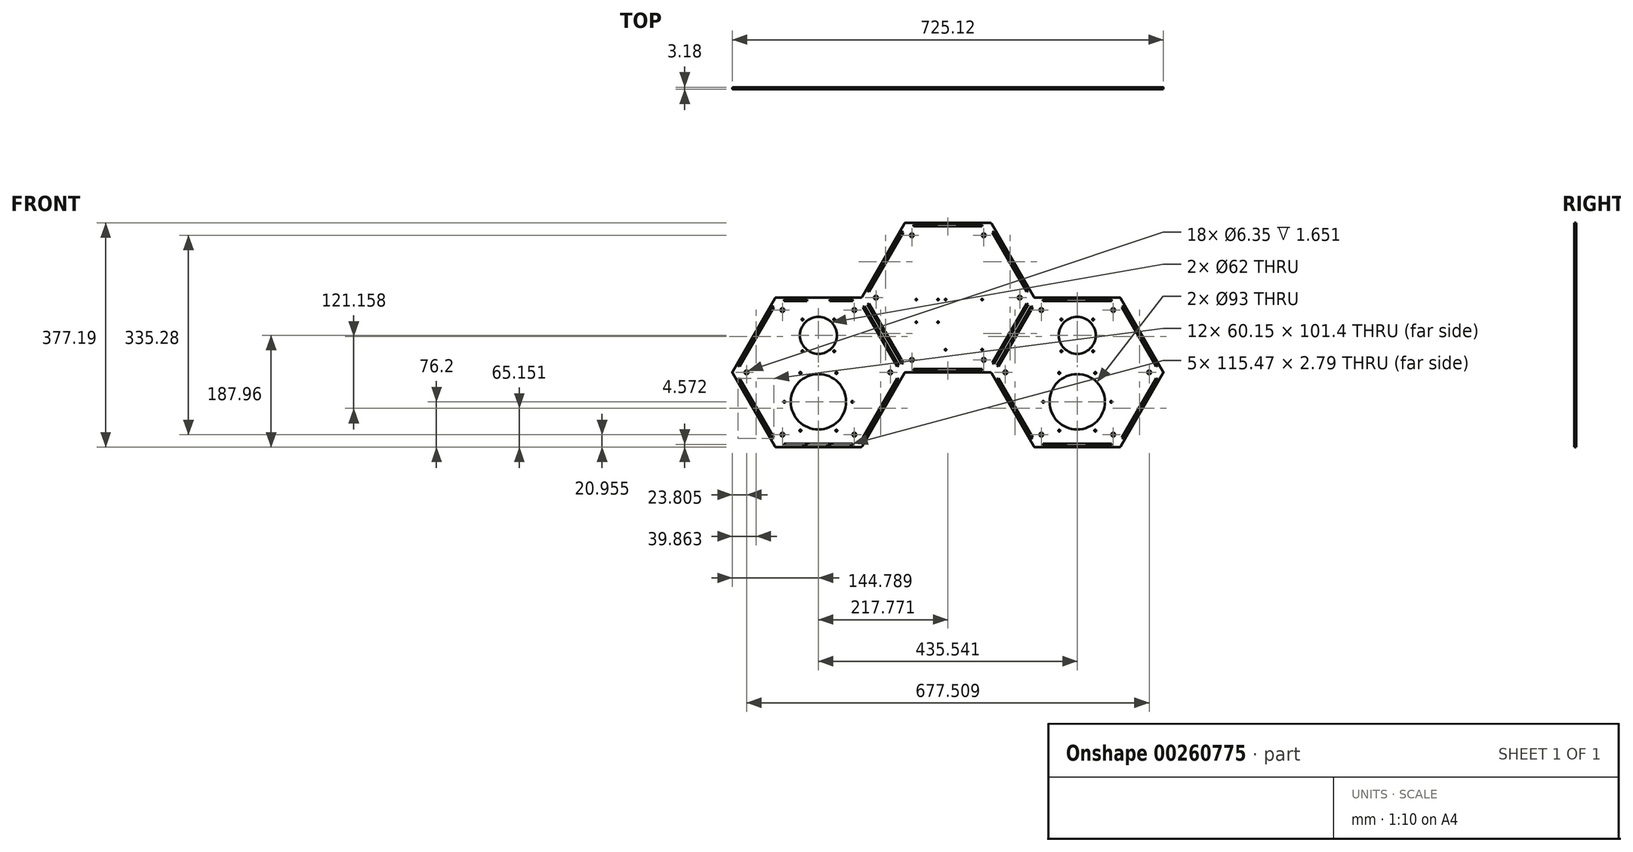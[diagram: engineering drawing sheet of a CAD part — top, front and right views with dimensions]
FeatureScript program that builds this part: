
annotation { "Feature Type Name" : "Feature", "Feature Type Description" : "" }
export const myFeature = defineFeature(function(context is Context, id is Id, definition is map)
    precondition{}
    {
        {
            var Q0;
            Q0=qCreatedBy(makeId("Front.planeOp"),FACE);
            var sketch = newSketch(context, id + "F0", { "sketchPlane" : qUnion([Q0])});
            skCircle(sketch, "E0.cCircle", {"center": v(0, 0) * mm, "radius": 125.73 * mm, "construction": true});
            skLineSegment(sketch, "E0.1", {"start": v(71.12, -125.73) * mm, "end": v(-71.12, -125.73) * mm});
            skLineSegment(sketch, "E0.3", {"start": v(-144.45, 1.27) * mm, "end": v(-73.32, 124.46) * mm});
            skLineSegment(sketch, "E0.4", {"start": v(-71.12, 125.73) * mm, "end": v(71.12, 125.73) * mm});
            skLineSegment(sketch, "E0.5", {"start": v(73.32, 124.46) * mm, "end": v(144.45, 1.27) * mm});
            skCircle(sketch, "E1.cCircle", {"center": v(-217.77, -125.73) * mm, "radius": 125.73 * mm, "construction": true});
            skLineSegment(sketch, "E1.0", {"start": v(-146.65, -251.46) * mm, "end": v(-288.9, -251.46) * mm});
            skLineSegment(sketch, "E1.1", {"start": v(-291.1, -250.19) * mm, "end": v(-362.22, -127) * mm});
            skLineSegment(sketch, "E1.2", {"start": v(-362.22, -124.46) * mm, "end": v(-291.1, -1.27) * mm});
            skLineSegment(sketch, "E1.3", {"start": v(-288.9, 0) * mm, "end": v(-146.65, 0) * mm});
            skLineSegment(sketch, "E1.5", {"start": v(-73.32, -127) * mm, "end": v(-144.45, -250.19) * mm});
            skPoint(sketch, "E1.0.midPoint", {"position": v(-217.77, -251.46) * mm});
            skCircle(sketch, "E2.cCircle", {"center": v(217.77, -125.73) * mm, "radius": 125.73 * mm, "construction": true});
            skLineSegment(sketch, "E2.0", {"start": v(362.22, -127) * mm, "end": v(291.1, -250.2) * mm});
            skLineSegment(sketch, "E2.1", {"start": v(288.9, -251.46) * mm, "end": v(146.65, -251.46) * mm});
            skLineSegment(sketch, "E2.2", {"start": v(144.45, -250.2) * mm, "end": v(73.32, -127) * mm});
            skLineSegment(sketch, "E2.4", {"start": v(146.65, 0) * mm, "end": v(288.9, 0) * mm});
            skLineSegment(sketch, "E2.5", {"start": v(291.1, -1.27) * mm, "end": v(362.22, -124.46) * mm});
            skPoint(sketch, "E2.0.midPoint", {"position": v(326.66, -188.6) * mm});
            skPoint(sketch, "E3.visualSharp", {"position": v(-72.6, 125.73) * mm});
            skArc(sketch, "E3.filletArc", {"start": v(-71.12, 125.73) * mm, "mid": v(-72.4, 125.39) * mm, "end": v(-73.32, 124.46) * mm});
            skPoint(sketch, "E4.visualSharp", {"position": v(72.6, 125.73) * mm});
            skArc(sketch, "E4.filletArc", {"start": v(73.32, 124.46) * mm, "mid": v(72.4, 125.39) * mm, "end": v(71.12, 125.73) * mm});
            skPoint(sketch, "E5.visualSharp", {"position": v(145.18, 0) * mm});
            skArc(sketch, "E5.filletArc", {"start": v(144.45, 1.27) * mm, "mid": v(145.38, 0.34) * mm, "end": v(146.65, 0) * mm});
            skPoint(sketch, "E6.visualSharp", {"position": v(290.36, 0) * mm});
            skArc(sketch, "E6.filletArc", {"start": v(291.1, -1.27) * mm, "mid": v(290.16, -0.34) * mm, "end": v(288.9, 0) * mm});
            skPoint(sketch, "E7.visualSharp", {"position": v(362.95, -125.73) * mm});
            skArc(sketch, "E7.filletArc", {"start": v(362.22, -127) * mm, "mid": v(362.56, -125.73) * mm, "end": v(362.22, -124.46) * mm});
            skPoint(sketch, "E8.visualSharp", {"position": v(290.36, -251.46) * mm});
            skArc(sketch, "E8.filletArc", {"start": v(288.9, -251.46) * mm, "mid": v(290.16, -251.12) * mm, "end": v(291.1, -250.2) * mm});
            skPoint(sketch, "E9.visualSharp", {"position": v(145.18, -251.46) * mm});
            skArc(sketch, "E9.filletArc", {"start": v(144.45, -250.2) * mm, "mid": v(145.38, -251.12) * mm, "end": v(146.65, -251.46) * mm});
            skPoint(sketch, "E10.visualSharp", {"position": v(72.6, -125.73) * mm});
            skArc(sketch, "E10.filletArc", {"start": v(73.32, -127) * mm, "mid": v(72.4, -126.07) * mm, "end": v(71.12, -125.73) * mm});
            skPoint(sketch, "E11.visualSharp", {"position": v(-72.6, -125.73) * mm});
            skArc(sketch, "E11.filletArc", {"start": v(-71.12, -125.73) * mm, "mid": v(-72.4, -126.07) * mm, "end": v(-73.32, -127) * mm});
            skPoint(sketch, "E12.visualSharp", {"position": v(-145.18, -251.46) * mm});
            skArc(sketch, "E12.filletArc", {"start": v(-146.65, -251.46) * mm, "mid": v(-145.38, -251.12) * mm, "end": v(-144.45, -250.19) * mm});
            skPoint(sketch, "E13.visualSharp", {"position": v(-290.36, -251.46) * mm});
            skArc(sketch, "E13.filletArc", {"start": v(-291.1, -250.19) * mm, "mid": v(-290.16, -251.12) * mm, "end": v(-288.9, -251.46) * mm});
            skPoint(sketch, "E14.visualSharp", {"position": v(-362.95, -125.73) * mm});
            skArc(sketch, "E14.filletArc", {"start": v(-362.22, -124.46) * mm, "mid": v(-362.56, -125.73) * mm, "end": v(-362.22, -127) * mm});
            skPoint(sketch, "E15.visualSharp", {"position": v(-290.36, 0) * mm});
            skArc(sketch, "E15.filletArc", {"start": v(-288.9, 0) * mm, "mid": v(-290.16, -0.34) * mm, "end": v(-291.1, -1.27) * mm});
            skPoint(sketch, "E16.visualSharp", {"position": v(-145.18, 0) * mm});
            skArc(sketch, "E16.filletArc", {"start": v(-146.65, 0) * mm, "mid": v(-145.38, 0.34) * mm, "end": v(-144.45, 1.27) * mm});
            skCircle(sketch, "E17.cCircle", {"center": v(-217.77, -125.73) * mm, "radius": 104.78 * mm, "construction": true});
            skLineSegment(sketch, "E17.0", {"start": v(-278.26, -20.95) * mm, "end": v(-157.28, -20.96) * mm, "construction": true});
            skLineSegment(sketch, "E17.1", {"start": v(-157.28, -20.95) * mm, "end": v(-96.79, -125.73) * mm, "construction": true});
            skLineSegment(sketch, "E17.2", {"start": v(-96.79, -125.73) * mm, "end": v(-157.28, -230.5) * mm, "construction": true});
            skLineSegment(sketch, "E17.3", {"start": v(-157.28, -230.5) * mm, "end": v(-278.26, -230.5) * mm, "construction": true});
            skLineSegment(sketch, "E17.4", {"start": v(-278.26, -230.5) * mm, "end": v(-338.75, -125.73) * mm, "construction": true});
            skLineSegment(sketch, "E17.5", {"start": v(-338.75, -125.73) * mm, "end": v(-278.26, -20.96) * mm, "construction": true});
            skPoint(sketch, "E17.0.midPoint", {"position": v(-217.77, -20.96) * mm});
            skCircle(sketch, "E18.cCircle", {"center": v(0, 0) * mm, "radius": 104.78 * mm, "construction": true});
            skLineSegment(sketch, "E18.0", {"start": v(60.5, 104.78) * mm, "end": v(120.98, 0) * mm, "construction": true});
            skLineSegment(sketch, "E18.1", {"start": v(120.98, 0) * mm, "end": v(60.5, -104.77) * mm, "construction": true});
            skLineSegment(sketch, "E18.2", {"start": v(60.5, -104.77) * mm, "end": v(-60.5, -104.78) * mm, "construction": true});
            skLineSegment(sketch, "E18.3", {"start": v(-60.5, -104.78) * mm, "end": v(-120.98, 0) * mm, "construction": true});
            skLineSegment(sketch, "E18.4", {"start": v(-120.98, 0) * mm, "end": v(-60.5, 104.78) * mm, "construction": true});
            skLineSegment(sketch, "E18.5", {"start": v(-60.5, 104.77) * mm, "end": v(60.5, 104.77) * mm, "construction": true});
            skPoint(sketch, "E18.0.midPoint", {"position": v(90.74, 52.39) * mm});
            skCircle(sketch, "E19.cCircle", {"center": v(217.77, -125.73) * mm, "radius": 104.78 * mm, "construction": true});
            skLineSegment(sketch, "E19.0", {"start": v(157.28, -20.96) * mm, "end": v(278.26, -20.96) * mm, "construction": true});
            skLineSegment(sketch, "E19.1", {"start": v(278.26, -20.96) * mm, "end": v(338.75, -125.73) * mm, "construction": true});
            skLineSegment(sketch, "E19.2", {"start": v(338.75, -125.73) * mm, "end": v(278.26, -230.5) * mm, "construction": true});
            skLineSegment(sketch, "E19.3", {"start": v(278.26, -230.5) * mm, "end": v(157.28, -230.5) * mm, "construction": true});
            skLineSegment(sketch, "E19.4", {"start": v(157.28, -230.5) * mm, "end": v(96.79, -125.73) * mm, "construction": true});
            skLineSegment(sketch, "E19.5", {"start": v(96.79, -125.73) * mm, "end": v(157.28, -20.96) * mm, "construction": true});
            skPoint(sketch, "E19.0.midPoint", {"position": v(217.77, -20.96) * mm});
            skCircle(sketch, "E20", {"center": v(-278.26, -20.96) * mm, "radius": 3.18 * mm});
            skCircle(sketch, "E21", {"center": v(-157.28, -20.95) * mm, "radius": 3.18 * mm});
            skCircle(sketch, "E22", {"center": v(-338.75, -125.73) * mm, "radius": 3.18 * mm});
            skCircle(sketch, "E23", {"center": v(-278.26, -230.5) * mm, "radius": 3.18 * mm});
            skCircle(sketch, "E24", {"center": v(-157.28, -230.5) * mm, "radius": 3.18 * mm});
            skCircle(sketch, "E25", {"center": v(-96.79, -125.73) * mm, "radius": 3.18 * mm});
            skCircle(sketch, "E26", {"center": v(-60.5, -104.78) * mm, "radius": 3.18 * mm});
            skCircle(sketch, "E27", {"center": v(-120.98, 0) * mm, "radius": 3.18 * mm});
            skCircle(sketch, "E28", {"center": v(-60.5, 104.77) * mm, "radius": 3.18 * mm});
            skCircle(sketch, "E29", {"center": v(60.5, 104.77) * mm, "radius": 3.18 * mm});
            skCircle(sketch, "E30", {"center": v(120.98, 0) * mm, "radius": 3.18 * mm});
            skCircle(sketch, "E31", {"center": v(60.5, -104.77) * mm, "radius": 3.18 * mm});
            skCircle(sketch, "E32", {"center": v(96.79, -125.73) * mm, "radius": 3.18 * mm});
            skCircle(sketch, "E33", {"center": v(157.28, -20.96) * mm, "radius": 3.18 * mm});
            skCircle(sketch, "E34", {"center": v(278.26, -20.96) * mm, "radius": 3.18 * mm});
            skCircle(sketch, "E35", {"center": v(338.75, -125.73) * mm, "radius": 3.18 * mm});
            skCircle(sketch, "E36", {"center": v(278.26, -230.5) * mm, "radius": 3.18 * mm});
            skCircle(sketch, "E37", {"center": v(157.28, -230.5) * mm, "radius": 3.18 * mm});
            skSolve(sketch);
        }
        {
            var Q0;
            Q0=makeQuery(id+"F0.imprint","IMPRINT",FACE,{"disambiguationData":[TD([[makeQuery(id+"F0.imprint","IMPRINT",EDGE,{"derivedFrom":sQuery(id+"F0.wireOp",EDGE,"E0.1")}),-1.0]])]});
            extrude(context, id + "F1", {"entities" : qUnion([Q0]), "depth" : 3.17 * mm});
        }
        {
            var Q0;
            Q0=makeQuery(id+"F0.imprint","IMPRINT",FACE,{"disambiguationData":[TD([[makeQuery(id+"F0.imprint","IMPRINT",EDGE,{"derivedFrom":sQuery(id+"F0.wireOp",EDGE,"E30")}),1.0]])]});
            var Q1;
            Q1=makeQuery(id+"F0.imprint","IMPRINT",FACE,{"disambiguationData":[TD([[makeQuery(id+"F0.imprint","IMPRINT",EDGE,{"derivedFrom":sQuery(id+"F0.wireOp",EDGE,"E33")}),1.0]])]});
            var Q2;
            Q2=makeQuery(id+"F0.imprint","IMPRINT",FACE,{"disambiguationData":[TD([[makeQuery(id+"F0.imprint","IMPRINT",EDGE,{"derivedFrom":sQuery(id+"F0.wireOp",EDGE,"E34")}),1.0]])]});
            var Q3;
            Q3=makeQuery(id+"F0.imprint","IMPRINT",FACE,{"disambiguationData":[TD([[makeQuery(id+"F0.imprint","IMPRINT",EDGE,{"derivedFrom":sQuery(id+"F0.wireOp",EDGE,"E35")}),1.0]])]});
            var Q4;
            Q4=makeQuery(id+"F0.imprint","IMPRINT",FACE,{"disambiguationData":[TD([[makeQuery(id+"F0.imprint","IMPRINT",EDGE,{"derivedFrom":sQuery(id+"F0.wireOp",EDGE,"E36")}),1.0]])]});
            var Q5;
            Q5=makeQuery(id+"F0.imprint","IMPRINT",FACE,{"disambiguationData":[TD([[makeQuery(id+"F0.imprint","IMPRINT",EDGE,{"derivedFrom":sQuery(id+"F0.wireOp",EDGE,"E37")}),1.0]])]});
            var Q6;
            Q6=makeQuery(id+"F0.imprint","IMPRINT",FACE,{"disambiguationData":[TD([[makeQuery(id+"F0.imprint","IMPRINT",EDGE,{"derivedFrom":sQuery(id+"F0.wireOp",EDGE,"E32")}),1.0]])]});
            var Q7;
            Q7=makeQuery(id+"F0.imprint","IMPRINT",FACE,{"disambiguationData":[TD([[makeQuery(id+"F0.imprint","IMPRINT",EDGE,{"derivedFrom":sQuery(id+"F0.wireOp",EDGE,"E31")}),1.0]])]});
            var Q8;
            Q8=makeQuery(id+"F0.imprint","IMPRINT",FACE,{"disambiguationData":[TD([[makeQuery(id+"F0.imprint","IMPRINT",EDGE,{"derivedFrom":sQuery(id+"F0.wireOp",EDGE,"E26")}),1.0]])]});
            var Q9;
            Q9=makeQuery(id+"F0.imprint","IMPRINT",FACE,{"disambiguationData":[TD([[makeQuery(id+"F0.imprint","IMPRINT",EDGE,{"derivedFrom":sQuery(id+"F0.wireOp",EDGE,"E25")}),1.0]])]});
            var Q10;
            Q10=makeQuery(id+"F0.imprint","IMPRINT",FACE,{"disambiguationData":[TD([[makeQuery(id+"F0.imprint","IMPRINT",EDGE,{"derivedFrom":sQuery(id+"F0.wireOp",EDGE,"E24")}),1.0]])]});
            var Q11;
            Q11=makeQuery(id+"F0.imprint","IMPRINT",FACE,{"disambiguationData":[TD([[makeQuery(id+"F0.imprint","IMPRINT",EDGE,{"derivedFrom":sQuery(id+"F0.wireOp",EDGE,"E23")}),1.0]])]});
            var Q12;
            Q12=makeQuery(id+"F0.imprint","IMPRINT",FACE,{"disambiguationData":[TD([[makeQuery(id+"F0.imprint","IMPRINT",EDGE,{"derivedFrom":sQuery(id+"F0.wireOp",EDGE,"E22")}),1.0]])]});
            var Q13;
            Q13=makeQuery(id+"F0.imprint","IMPRINT",FACE,{"disambiguationData":[TD([[makeQuery(id+"F0.imprint","IMPRINT",EDGE,{"derivedFrom":sQuery(id+"F0.wireOp",EDGE,"E20")}),1.0]])]});
            var Q14;
            Q14=makeQuery(id+"F0.imprint","IMPRINT",FACE,{"disambiguationData":[TD([[makeQuery(id+"F0.imprint","IMPRINT",EDGE,{"derivedFrom":sQuery(id+"F0.wireOp",EDGE,"E21")}),1.0]])]});
            var Q15;
            Q15=makeQuery(id+"F0.imprint","IMPRINT",FACE,{"disambiguationData":[TD([[makeQuery(id+"F0.imprint","IMPRINT",EDGE,{"derivedFrom":sQuery(id+"F0.wireOp",EDGE,"E27")}),1.0]])]});
            var Q16;
            Q16=makeQuery(id+"F0.imprint","IMPRINT",FACE,{"disambiguationData":[TD([[makeQuery(id+"F0.imprint","IMPRINT",EDGE,{"derivedFrom":sQuery(id+"F0.wireOp",EDGE,"E28")}),1.0]])]});
            var Q17;
            Q17=makeQuery(id+"F0.imprint","IMPRINT",FACE,{"disambiguationData":[TD([[makeQuery(id+"F0.imprint","IMPRINT",EDGE,{"derivedFrom":sQuery(id+"F0.wireOp",EDGE,"E29")}),1.0]])]});
            extrude(context, id + "F2", {"entities" : qUnion([Q0, Q1, Q2, Q3, Q4, Q5, Q6, Q7, Q8, Q9, Q10, Q11, Q12, Q13, Q14, Q15, Q16, Q17]), "operationType" : NewBodyOperationType.ADD, "depth" : 1.52 * mm});
        }
        {
            var Q0;
            Q0=makeQuery(id+"F1.opExtrude","CAP_FACE",FACE,{"disambiguationData":[OSD([sQuery(id+"F0.wireOp",EDGE,"E0.1"),sQuery(id+"F0.wireOp",EDGE,"E0.3"),sQuery(id+"F0.wireOp",EDGE,"E0.4"),sQuery(id+"F0.wireOp",EDGE,"E0.5"),sQuery(id+"F0.wireOp",EDGE,"E1.0"),sQuery(id+"F0.wireOp",EDGE,"E1.1"),sQuery(id+"F0.wireOp",EDGE,"E1.2"),sQuery(id+"F0.wireOp",EDGE,"E1.3"),sQuery(id+"F0.wireOp",EDGE,"E1.5"),sQuery(id+"F0.wireOp",EDGE,"E2.0"),sQuery(id+"F0.wireOp",EDGE,"E2.1"),sQuery(id+"F0.wireOp",EDGE,"E2.2"),sQuery(id+"F0.wireOp",EDGE,"E2.4"),sQuery(id+"F0.wireOp",EDGE,"E2.5"),sQuery(id+"F0.wireOp",EDGE,"E3.filletArc"),sQuery(id+"F0.wireOp",EDGE,"E4.filletArc"),sQuery(id+"F0.wireOp",EDGE,"E5.filletArc"),sQuery(id+"F0.wireOp",EDGE,"E6.filletArc"),sQuery(id+"F0.wireOp",EDGE,"E7.filletArc"),sQuery(id+"F0.wireOp",EDGE,"E8.filletArc"),sQuery(id+"F0.wireOp",EDGE,"E9.filletArc"),sQuery(id+"F0.wireOp",EDGE,"E10.filletArc"),sQuery(id+"F0.wireOp",EDGE,"E11.filletArc"),sQuery(id+"F0.wireOp",EDGE,"E12.filletArc"),sQuery(id+"F0.wireOp",EDGE,"E13.filletArc"),sQuery(id+"F0.wireOp",EDGE,"E14.filletArc"),sQuery(id+"F0.wireOp",EDGE,"E15.filletArc"),sQuery(id+"F0.wireOp",EDGE,"E16.filletArc"),sQuery(id+"F0.wireOp",EDGE,"E20"),sQuery(id+"F0.wireOp",EDGE,"E21"),sQuery(id+"F0.wireOp",EDGE,"E22"),sQuery(id+"F0.wireOp",EDGE,"E23"),sQuery(id+"F0.wireOp",EDGE,"E24"),sQuery(id+"F0.wireOp",EDGE,"E25"),sQuery(id+"F0.wireOp",EDGE,"E26"),sQuery(id+"F0.wireOp",EDGE,"E27"),sQuery(id+"F0.wireOp",EDGE,"E28"),sQuery(id+"F0.wireOp",EDGE,"E29"),sQuery(id+"F0.wireOp",EDGE,"E30"),sQuery(id+"F0.wireOp",EDGE,"E31"),sQuery(id+"F0.wireOp",EDGE,"E32"),sQuery(id+"F0.wireOp",EDGE,"E33"),sQuery(id+"F0.wireOp",EDGE,"E34"),sQuery(id+"F0.wireOp",EDGE,"E35"),sQuery(id+"F0.wireOp",EDGE,"E36"),sQuery(id+"F0.wireOp",EDGE,"E37")])],"isStart":false});
            var sketch = newSketch(context, id + "F3", { "sketchPlane" : qUnion([Q0])});
            skPoint(sketch, "E38", {"position": v(-217.77, -127) * mm});
            skCircle(sketch, "E39", {"center": v(-217.77, -63.5) * mm, "radius": 31 * mm});
            skCircle(sketch, "E40", {"center": v(-217.77, -175.26) * mm, "radius": 46.5 * mm});
            skLineSegment(sketch, "E41", {"start": v(-295.75, -175.26) * mm, "end": v(-133.33, -175.26) * mm, "construction": true});
            skCircle(sketch, "E42", {"center": v(-217.77, -175.26) * mm, "radius": 61.65 * mm, "construction": true});
            skCircle(sketch, "E43", {"center": v(-217.77, -175.26) * mm, "radius": 57.15 * mm, "construction": true});
            skCircle(sketch, "E44", {"center": v(-160.62, -175.26) * mm, "radius": 1.52 * mm});
            skLineSegment(sketch, "E45", {"start": v(-217.77, -175.26) * mm, "end": v(-217.77, -149.19) * mm, "construction": true});
            skLineSegment(sketch, "E46", {"start": v(-217.77, -175.26) * mm, "end": v(-187.49, -126.8) * mm, "construction": true});
            skLineSegment(sketch, "E47", {"start": v(-217.77, -175.26) * mm, "end": v(-187.49, -223.73) * mm, "construction": true});
            skCircle(sketch, "E48", {"center": v(-187.49, -126.8) * mm, "radius": 1.52 * mm});
            skCircle(sketch, "E49", {"center": v(-187.49, -223.73) * mm, "radius": 1.52 * mm});
            skCircle(sketch, "E50.MirrorC", {"center": v(-248.06, -126.8) * mm, "radius": 1.52 * mm});
            skCircle(sketch, "E51.MirrorC", {"center": v(-248.06, -223.73) * mm, "radius": 1.52 * mm});
            skCircle(sketch, "E52.MirrorC", {"center": v(-274.92, -175.26) * mm, "radius": 1.52 * mm});
            skCircle(sketch, "E53", {"center": v(-217.77, -63.5) * mm, "radius": 37.72 * mm, "construction": true});
            skLineSegment(sketch, "E54", {"start": v(-217.77, -63.5) * mm, "end": v(-244.44, -36.83) * mm, "construction": true});
            skCircle(sketch, "E55", {"center": v(-244.44, -36.83) * mm, "radius": 1.52 * mm});
            skCircle(sketch, "E56", {"center": v(-244.44, -90.17) * mm, "radius": 1.52 * mm});
            skCircle(sketch, "E57", {"center": v(-191.1, -90.17) * mm, "radius": 1.52 * mm});
            skCircle(sketch, "E58", {"center": v(-191.1, -36.83) * mm, "radius": 1.52 * mm});
            skLineSegment(sketch, "E59", {"start": v(-244.44, -36.83) * mm, "end": v(-191.1, -36.83) * mm, "construction": true});
            skCircle(sketch, "E60.MirrorC", {"center": v(160.62, -175.26) * mm, "radius": 1.52 * mm});
            skCircle(sketch, "E61.MirrorC", {"center": v(187.49, -223.73) * mm, "radius": 1.52 * mm});
            skCircle(sketch, "E62.MirrorC", {"center": v(248.06, -223.73) * mm, "radius": 1.52 * mm});
            skCircle(sketch, "E63.MirrorC", {"center": v(274.92, -175.26) * mm, "radius": 1.52 * mm});
            skCircle(sketch, "E64.MirrorC", {"center": v(187.49, -126.8) * mm, "radius": 1.52 * mm});
            skCircle(sketch, "E65.MirrorC", {"center": v(248.06, -126.8) * mm, "radius": 1.52 * mm});
            skCircle(sketch, "E66.MirrorC", {"center": v(217.77, -175.26) * mm, "radius": 46.5 * mm});
            skCircle(sketch, "E67.MirrorC", {"center": v(244.44, -90.17) * mm, "radius": 1.52 * mm});
            skCircle(sketch, "E68.MirrorC", {"center": v(191.1, -90.17) * mm, "radius": 1.52 * mm});
            skCircle(sketch, "E69.MirrorC", {"center": v(191.1, -36.83) * mm, "radius": 1.52 * mm});
            skCircle(sketch, "E70.MirrorC", {"center": v(217.77, -63.5) * mm, "radius": 31 * mm});
            skCircle(sketch, "E71.MirrorC", {"center": v(244.44, -36.83) * mm, "radius": 1.52 * mm});
            skSolve(sketch);
        }
        {
            var Q0;
            Q0 = qSketchRegion(id + "F3", true);
            extrude(context, id + "F4", {"entities" : qUnion([Q0]), "operationType" : NewBodyOperationType.REMOVE, "endBound" : BoundingType.THROUGH_ALL, "oppositeDirection" : true, "depth" : 25.4 * mm});
        }
        {
            var Q0;
            Q0=makeQuery(id+"F1.opExtrude","CAP_FACE",FACE,{"disambiguationData":[OSD([sQuery(id+"F0.wireOp",EDGE,"E0.1"),sQuery(id+"F0.wireOp",EDGE,"E0.3"),sQuery(id+"F0.wireOp",EDGE,"E0.4"),sQuery(id+"F0.wireOp",EDGE,"E0.5"),sQuery(id+"F0.wireOp",EDGE,"E1.0"),sQuery(id+"F0.wireOp",EDGE,"E1.1"),sQuery(id+"F0.wireOp",EDGE,"E1.2"),sQuery(id+"F0.wireOp",EDGE,"E1.3"),sQuery(id+"F0.wireOp",EDGE,"E1.5"),sQuery(id+"F0.wireOp",EDGE,"E2.0"),sQuery(id+"F0.wireOp",EDGE,"E2.1"),sQuery(id+"F0.wireOp",EDGE,"E2.2"),sQuery(id+"F0.wireOp",EDGE,"E2.4"),sQuery(id+"F0.wireOp",EDGE,"E2.5"),sQuery(id+"F0.wireOp",EDGE,"E3.filletArc"),sQuery(id+"F0.wireOp",EDGE,"E4.filletArc"),sQuery(id+"F0.wireOp",EDGE,"E5.filletArc"),sQuery(id+"F0.wireOp",EDGE,"E6.filletArc"),sQuery(id+"F0.wireOp",EDGE,"E7.filletArc"),sQuery(id+"F0.wireOp",EDGE,"E8.filletArc"),sQuery(id+"F0.wireOp",EDGE,"E9.filletArc"),sQuery(id+"F0.wireOp",EDGE,"E10.filletArc"),sQuery(id+"F0.wireOp",EDGE,"E11.filletArc"),sQuery(id+"F0.wireOp",EDGE,"E12.filletArc"),sQuery(id+"F0.wireOp",EDGE,"E13.filletArc"),sQuery(id+"F0.wireOp",EDGE,"E14.filletArc"),sQuery(id+"F0.wireOp",EDGE,"E15.filletArc"),sQuery(id+"F0.wireOp",EDGE,"E16.filletArc"),sQuery(id+"F0.wireOp",EDGE,"E20"),sQuery(id+"F0.wireOp",EDGE,"E21"),sQuery(id+"F0.wireOp",EDGE,"E22"),sQuery(id+"F0.wireOp",EDGE,"E23"),sQuery(id+"F0.wireOp",EDGE,"E24"),sQuery(id+"F0.wireOp",EDGE,"E25"),sQuery(id+"F0.wireOp",EDGE,"E26"),sQuery(id+"F0.wireOp",EDGE,"E27"),sQuery(id+"F0.wireOp",EDGE,"E28"),sQuery(id+"F0.wireOp",EDGE,"E29"),sQuery(id+"F0.wireOp",EDGE,"E30"),sQuery(id+"F0.wireOp",EDGE,"E31"),sQuery(id+"F0.wireOp",EDGE,"E32"),sQuery(id+"F0.wireOp",EDGE,"E33"),sQuery(id+"F0.wireOp",EDGE,"E34"),sQuery(id+"F0.wireOp",EDGE,"E35"),sQuery(id+"F0.wireOp",EDGE,"E36"),sQuery(id+"F0.wireOp",EDGE,"E37")])],"isStart":false});
            var sketch = newSketch(context, id + "F5", { "sketchPlane" : qUnion([Q0])});
            skPoint(sketch, "E72", {"position": v(-217.77, -125.73) * mm});
            skCircle(sketch, "E73.cCircle", {"center": v(-217.77, -125.73) * mm, "radius": 125.73 * mm, "construction": true});
            skLineSegment(sketch, "E73.0", {"start": v(-275.7, 0) * mm, "end": v(-159.85, 0) * mm, "construction": true});
            skLineSegment(sketch, "E73.1", {"start": v(-137.85, -12.7) * mm, "end": v(-79.92, -113.03) * mm, "construction": true});
            skLineSegment(sketch, "E73.2", {"start": v(-79.92, -138.43) * mm, "end": v(-137.85, -238.76) * mm, "construction": true});
            skLineSegment(sketch, "E73.3", {"start": v(-159.85, -251.46) * mm, "end": v(-275.7, -251.46) * mm, "construction": true});
            skLineSegment(sketch, "E73.4", {"start": v(-297.7, -238.76) * mm, "end": v(-355.62, -138.43) * mm, "construction": true});
            skLineSegment(sketch, "E73.5", {"start": v(-355.62, -113.03) * mm, "end": v(-297.7, -12.7) * mm, "construction": true});
            skPoint(sketch, "E73.0.midPoint", {"position": v(-217.77, 0) * mm});
            skPoint(sketch, "E74.visualSharp", {"position": v(-290.36, 0) * mm});
            skArc(sketch, "E74.filletArc", {"start": v(-275.7, 0) * mm, "mid": v(-288.4, -3.4) * mm, "end": v(-297.7, -12.7) * mm, "construction": true});
            skPoint(sketch, "E75.visualSharp", {"position": v(-145.18, 0) * mm});
            skArc(sketch, "E75.filletArc", {"start": v(-137.85, -12.7) * mm, "mid": v(-147.15, -3.4) * mm, "end": v(-159.85, 0) * mm, "construction": true});
            skPoint(sketch, "E76.visualSharp", {"position": v(-72.6, -125.73) * mm});
            skArc(sketch, "E76.filletArc", {"start": v(-79.92, -138.43) * mm, "mid": v(-76.52, -125.73) * mm, "end": v(-79.92, -113.03) * mm, "construction": true});
            skPoint(sketch, "E77.visualSharp", {"position": v(-145.18, -251.46) * mm});
            skArc(sketch, "E77.filletArc", {"start": v(-159.85, -251.46) * mm, "mid": v(-147.15, -248.06) * mm, "end": v(-137.85, -238.76) * mm, "construction": true});
            skPoint(sketch, "E78.visualSharp", {"position": v(-290.36, -251.46) * mm});
            skArc(sketch, "E78.filletArc", {"start": v(-297.7, -238.76) * mm, "mid": v(-288.4, -248.06) * mm, "end": v(-275.7, -251.46) * mm, "construction": true});
            skPoint(sketch, "E79.visualSharp", {"position": v(-362.95, -125.73) * mm});
            skArc(sketch, "E79.filletArc", {"start": v(-355.62, -113.03) * mm, "mid": v(-359.02, -125.73) * mm, "end": v(-355.62, -138.43) * mm, "construction": true});
            skLineSegment(sketch, "E80.bottom", {"start": v(-275.5, -5.97) * mm, "end": v(-160.04, -5.97) * mm});
            skLineSegment(sketch, "E80.top", {"start": v(-275.5, -3.18) * mm, "end": v(-160.04, -3.18) * mm});
            skLineSegment(sketch, "E80.left", {"start": v(-275.5, -3.18) * mm, "end": v(-275.5, -5.97) * mm});
            skLineSegment(sketch, "E80.right", {"start": v(-160.04, -3.18) * mm, "end": v(-160.04, -5.97) * mm});
            skLineSegment(sketch, "E81.1.0", {"start": v(-352.77, -114.45) * mm, "end": v(-295.04, -14.45) * mm});
            skLineSegment(sketch, "E81.1.1", {"start": v(-352.77, -114.45) * mm, "end": v(-350.35, -115.85) * mm});
            skLineSegment(sketch, "E81.1.2", {"start": v(-350.35, -115.85) * mm, "end": v(-292.62, -15.85) * mm});
            skLineSegment(sketch, "E81.1.3", {"start": v(-295.04, -14.45) * mm, "end": v(-292.62, -15.85) * mm});
            skLineSegment(sketch, "E81.2.0", {"start": v(-295.04, -237) * mm, "end": v(-352.77, -137) * mm});
            skLineSegment(sketch, "E81.2.1", {"start": v(-295.04, -237) * mm, "end": v(-292.62, -235.61) * mm});
            skLineSegment(sketch, "E81.2.2", {"start": v(-292.62, -235.61) * mm, "end": v(-350.35, -135.61) * mm});
            skLineSegment(sketch, "E81.2.3", {"start": v(-352.77, -137) * mm, "end": v(-350.35, -135.61) * mm});
            skLineSegment(sketch, "E81.3.0", {"start": v(-160.04, -248.28) * mm, "end": v(-275.5, -248.28) * mm});
            skLineSegment(sketch, "E81.3.1", {"start": v(-160.04, -248.28) * mm, "end": v(-160.04, -245.5) * mm});
            skLineSegment(sketch, "E81.3.2", {"start": v(-160.04, -245.5) * mm, "end": v(-275.5, -245.5) * mm});
            skLineSegment(sketch, "E81.3.3", {"start": v(-275.5, -248.28) * mm, "end": v(-275.5, -245.5) * mm});
            skLineSegment(sketch, "E81.4.0", {"start": v(-82.77, -137) * mm, "end": v(-140.5, -237) * mm});
            skLineSegment(sketch, "E81.4.1", {"start": v(-82.77, -137) * mm, "end": v(-85.19, -135.61) * mm});
            skLineSegment(sketch, "E81.4.2", {"start": v(-85.19, -135.61) * mm, "end": v(-142.92, -235.61) * mm});
            skLineSegment(sketch, "E81.4.3", {"start": v(-140.5, -237) * mm, "end": v(-142.92, -235.61) * mm});
            skLineSegment(sketch, "E81.5.0", {"start": v(-140.5, -14.45) * mm, "end": v(-82.77, -114.45) * mm});
            skLineSegment(sketch, "E81.5.1", {"start": v(-140.5, -14.45) * mm, "end": v(-142.92, -15.85) * mm});
            skLineSegment(sketch, "E81.5.2", {"start": v(-142.92, -15.85) * mm, "end": v(-85.19, -115.85) * mm});
            skLineSegment(sketch, "E81.5.3", {"start": v(-82.77, -114.45) * mm, "end": v(-85.19, -115.85) * mm});
            skLineSegment(sketch, "E82.MirrorCS", {"start": v(140.5, -14.45) * mm, "end": v(142.92, -15.85) * mm});
            skLineSegment(sketch, "E83.MirrorCS", {"start": v(140.5, -14.45) * mm, "end": v(82.77, -114.45) * mm});
            skLineSegment(sketch, "E84.MirrorCS", {"start": v(142.92, -15.85) * mm, "end": v(85.19, -115.85) * mm});
            skLineSegment(sketch, "E85.MirrorCS", {"start": v(82.77, -114.45) * mm, "end": v(85.19, -115.85) * mm});
            skLineSegment(sketch, "E86.MirrorCS", {"start": v(82.77, -137) * mm, "end": v(85.19, -135.61) * mm});
            skLineSegment(sketch, "E87.MirrorCS", {"start": v(85.19, -135.61) * mm, "end": v(142.92, -235.61) * mm});
            skLineSegment(sketch, "E88.MirrorCS", {"start": v(82.77, -137) * mm, "end": v(140.5, -237) * mm});
            skLineSegment(sketch, "E89.MirrorCS", {"start": v(140.5, -237) * mm, "end": v(142.92, -235.61) * mm});
            skLineSegment(sketch, "E90.MirrorCS", {"start": v(160.04, -248.28) * mm, "end": v(160.04, -245.5) * mm});
            skLineSegment(sketch, "E91.MirrorCS", {"start": v(160.04, -248.28) * mm, "end": v(275.5, -248.28) * mm});
            skLineSegment(sketch, "E92.MirrorCS", {"start": v(160.04, -245.5) * mm, "end": v(275.5, -245.5) * mm});
            skLineSegment(sketch, "E93.MirrorCS", {"start": v(275.5, -248.28) * mm, "end": v(275.5, -245.5) * mm});
            skLineSegment(sketch, "E94.MirrorCS", {"start": v(295.04, -237) * mm, "end": v(292.62, -235.61) * mm});
            skLineSegment(sketch, "E95.MirrorCS", {"start": v(295.04, -237) * mm, "end": v(352.77, -137) * mm});
            skLineSegment(sketch, "E96.MirrorCS", {"start": v(292.62, -235.61) * mm, "end": v(350.35, -135.61) * mm});
            skLineSegment(sketch, "E97.MirrorCS", {"start": v(352.77, -137) * mm, "end": v(350.35, -135.61) * mm});
            skLineSegment(sketch, "E98.MirrorCS", {"start": v(352.77, -114.45) * mm, "end": v(350.35, -115.85) * mm});
            skLineSegment(sketch, "E99.MirrorCS", {"start": v(350.35, -115.85) * mm, "end": v(292.62, -15.85) * mm});
            skLineSegment(sketch, "E100.MirrorCS", {"start": v(352.77, -114.45) * mm, "end": v(295.04, -14.45) * mm});
            skLineSegment(sketch, "E101.MirrorCS", {"start": v(295.04, -14.45) * mm, "end": v(292.62, -15.85) * mm});
            skLineSegment(sketch, "E102.MirrorCS", {"start": v(275.5, -3.18) * mm, "end": v(275.5, -5.97) * mm});
            skLineSegment(sketch, "E103.MirrorCS", {"start": v(275.5, -5.97) * mm, "end": v(160.04, -5.97) * mm});
            skLineSegment(sketch, "E104.MirrorCS", {"start": v(275.5, -3.18) * mm, "end": v(160.04, -3.18) * mm});
            skLineSegment(sketch, "E105.MirrorCS", {"start": v(160.04, -3.18) * mm, "end": v(160.04, -5.97) * mm});
            skLineSegment(sketch, "E106.MirrorCS", {"start": v(57.74, -122.55) * mm, "end": v(57.74, -119.76) * mm});
            skLineSegment(sketch, "E107.MirrorCS", {"start": v(-57.74, -122.55) * mm, "end": v(57.74, -122.55) * mm});
            skLineSegment(sketch, "E108.MirrorCS", {"start": v(-57.74, -119.76) * mm, "end": v(57.74, -119.76) * mm});
            skLineSegment(sketch, "E109.MirrorCS", {"start": v(-57.74, -122.55) * mm, "end": v(-57.74, -119.76) * mm});
            skLineSegment(sketch, "E110.MirrorCS", {"start": v(-77.27, -111.28) * mm, "end": v(-74.85, -109.88) * mm});
            skLineSegment(sketch, "E111.MirrorCS", {"start": v(-132.58, -9.88) * mm, "end": v(-74.85, -109.88) * mm});
            skLineSegment(sketch, "E112.MirrorCS", {"start": v(-135, -11.28) * mm, "end": v(-77.27, -111.28) * mm});
            skLineSegment(sketch, "E113.MirrorCS", {"start": v(-135, -11.28) * mm, "end": v(-132.58, -9.88) * mm});
            skLineSegment(sketch, "E114.MirrorCS", {"start": v(-135, 11.28) * mm, "end": v(-132.58, 9.88) * mm});
            skLineSegment(sketch, "E115.MirrorCS", {"start": v(-74.85, 109.88) * mm, "end": v(-132.58, 9.88) * mm});
            skLineSegment(sketch, "E116.MirrorCS", {"start": v(-77.27, 111.28) * mm, "end": v(-135, 11.28) * mm});
            skLineSegment(sketch, "E117.MirrorCS", {"start": v(-77.27, 111.28) * mm, "end": v(-74.85, 109.88) * mm});
            skLineSegment(sketch, "E118.MirrorCS", {"start": v(-57.74, 122.55) * mm, "end": v(-57.74, 119.76) * mm});
            skLineSegment(sketch, "E119.MirrorCS", {"start": v(57.74, 119.76) * mm, "end": v(-57.74, 119.76) * mm});
            skLineSegment(sketch, "E120.MirrorCS", {"start": v(57.74, 122.56) * mm, "end": v(-57.74, 122.56) * mm});
            skLineSegment(sketch, "E121.MirrorCS", {"start": v(57.74, 122.56) * mm, "end": v(57.74, 119.76) * mm});
            skLineSegment(sketch, "E122.MirrorCS", {"start": v(77.27, 111.28) * mm, "end": v(74.85, 109.88) * mm});
            skLineSegment(sketch, "E123.MirrorCS", {"start": v(132.58, 9.88) * mm, "end": v(74.85, 109.88) * mm});
            skLineSegment(sketch, "E124.MirrorCS", {"start": v(135, 11.28) * mm, "end": v(77.27, 111.28) * mm});
            skLineSegment(sketch, "E125.MirrorCS", {"start": v(135, 11.28) * mm, "end": v(132.58, 9.88) * mm});
            skLineSegment(sketch, "E126.MirrorCS", {"start": v(135, -11.28) * mm, "end": v(132.58, -9.88) * mm});
            skLineSegment(sketch, "E127.MirrorCS", {"start": v(74.85, -109.88) * mm, "end": v(132.58, -9.88) * mm});
            skLineSegment(sketch, "E128.MirrorCS", {"start": v(77.27, -111.28) * mm, "end": v(74.85, -109.88) * mm});
            skLineSegment(sketch, "E129.MirrorCS", {"start": v(77.27, -111.28) * mm, "end": v(135, -11.28) * mm});
            skSolve(sketch);
        }
        {
            var Q0;
            Q0 = qSketchRegion(id + "F5", true);
            extrude(context, id + "F6", {"entities" : qUnion([Q0]), "operationType" : NewBodyOperationType.REMOVE, "endBound" : BoundingType.THROUGH_ALL, "oppositeDirection" : true, "depth" : 25.4 * mm});
        }
        {
            var Q0;
            {var subQ0=sQuery(id+"F0.wireOp",EDGE,"E25");var subQ1=sQuery(id+"F0.wireOp",EDGE,"E20");var subQ2=sQuery(id+"F0.wireOp",EDGE,"E21");var subQ3=sQuery(id+"F0.wireOp",EDGE,"E22");var subQ4=sQuery(id+"F0.wireOp",EDGE,"E23");var subQ5=sQuery(id+"F0.wireOp",EDGE,"E24");Q0=makeQuery(id+"F0aKffUkCtTZm95_1.boolean.opBoolean","SPLIT",FACE,{"disambiguationData":[TD([makeQuery(id+"F1.opExtrude","SWEPT_FACE",FACE,{"disambiguationData":[OSD([subQ1])]})])],"derivedFrom":makeQuery(id+"F1.opExtrude","CAP_FACE",FACE,{"disambiguationData":[OSD([sQuery(id+"F0.wireOp",EDGE,"E0.1"),sQuery(id+"F0.wireOp",EDGE,"E0.3"),sQuery(id+"F0.wireOp",EDGE,"E0.4"),sQuery(id+"F0.wireOp",EDGE,"E0.5"),sQuery(id+"F0.wireOp",EDGE,"E1.0"),sQuery(id+"F0.wireOp",EDGE,"E1.1"),sQuery(id+"F0.wireOp",EDGE,"E1.2"),sQuery(id+"F0.wireOp",EDGE,"E1.3"),sQuery(id+"F0.wireOp",EDGE,"E1.5"),sQuery(id+"F0.wireOp",EDGE,"E2.0"),sQuery(id+"F0.wireOp",EDGE,"E2.1"),sQuery(id+"F0.wireOp",EDGE,"E2.2"),sQuery(id+"F0.wireOp",EDGE,"E2.4"),sQuery(id+"F0.wireOp",EDGE,"E2.5"),sQuery(id+"F0.wireOp",EDGE,"E3.filletArc"),sQuery(id+"F0.wireOp",EDGE,"E4.filletArc"),sQuery(id+"F0.wireOp",EDGE,"E5.filletArc"),sQuery(id+"F0.wireOp",EDGE,"E6.filletArc"),sQuery(id+"F0.wireOp",EDGE,"E7.filletArc"),sQuery(id+"F0.wireOp",EDGE,"E8.filletArc"),sQuery(id+"F0.wireOp",EDGE,"E9.filletArc"),sQuery(id+"F0.wireOp",EDGE,"E10.filletArc"),sQuery(id+"F0.wireOp",EDGE,"E11.filletArc"),sQuery(id+"F0.wireOp",EDGE,"E12.filletArc"),sQuery(id+"F0.wireOp",EDGE,"E13.filletArc"),sQuery(id+"F0.wireOp",EDGE,"E14.filletArc"),sQuery(id+"F0.wireOp",EDGE,"E15.filletArc"),sQuery(id+"F0.wireOp",EDGE,"E16.filletArc"),subQ1,subQ2,subQ3,subQ4,subQ5,subQ0,sQuery(id+"F0.wireOp",EDGE,"E26"),sQuery(id+"F0.wireOp",EDGE,"E27"),sQuery(id+"F0.wireOp",EDGE,"E28"),sQuery(id+"F0.wireOp",EDGE,"E29"),sQuery(id+"F0.wireOp",EDGE,"E30"),sQuery(id+"F0.wireOp",EDGE,"E31"),sQuery(id+"F0.wireOp",EDGE,"E32"),sQuery(id+"F0.wireOp",EDGE,"E33"),sQuery(id+"F0.wireOp",EDGE,"E34"),sQuery(id+"F0.wireOp",EDGE,"E35"),sQuery(id+"F0.wireOp",EDGE,"E36"),sQuery(id+"F0.wireOp",EDGE,"E37")])],"isStart":false})});}
            var sketch = newSketch(context, id + "F7", { "sketchPlane" : qUnion([Q0])});
            skLineSegment(sketch, "E130.bottom", {"start": v(-237.07, -5.97) * mm, "end": v(-198.47, -5.97) * mm});
            skLineSegment(sketch, "E130.top", {"start": v(-237.07, -3.18) * mm, "end": v(-198.47, -3.18) * mm});
            skLineSegment(sketch, "E130.left", {"start": v(-237.07, -5.97) * mm, "end": v(-237.07, -3.18) * mm});
            skLineSegment(sketch, "E130.right", {"start": v(-198.47, -5.97) * mm, "end": v(-198.47, -3.18) * mm});
            skPoint(sketch, "E131", {"position": v(-217.77, -5.97) * mm});
            skSolve(sketch);
        }
        {
            var Q0;
            Q0 = qSketchRegion(id + "F7", true);
            var Q1;
            {var subQ0=sQuery(id+"F0.wireOp",EDGE,"E37");var subQ1=sQuery(id+"F0.wireOp",EDGE,"E36");var subQ2=sQuery(id+"F0.wireOp",EDGE,"E35");var subQ3=sQuery(id+"F0.wireOp",EDGE,"E34");var subQ4=sQuery(id+"F0.wireOp",EDGE,"E33");var subQ5=sQuery(id+"F0.wireOp",EDGE,"E32");var subQ6=sQuery(id+"F0.wireOp",EDGE,"E31");var subQ7=sQuery(id+"F0.wireOp",EDGE,"E30");var subQ8=sQuery(id+"F0.wireOp",EDGE,"E29");var subQ9=sQuery(id+"F0.wireOp",EDGE,"E28");var subQ10=sQuery(id+"F0.wireOp",EDGE,"E27");var subQ11=sQuery(id+"F0.wireOp",EDGE,"E26");var subQ12=sQuery(id+"F0.wireOp",EDGE,"E25");var subQ13=sQuery(id+"F0.wireOp",EDGE,"E24");var subQ14=sQuery(id+"F0.wireOp",EDGE,"E23");var subQ15=sQuery(id+"F0.wireOp",EDGE,"E22");var subQ16=sQuery(id+"F0.wireOp",EDGE,"E21");var subQ17=sQuery(id+"F0.wireOp",EDGE,"E20");Q1=makeQuery(id+"F2.boolean.opBoolean","MERGE",FACE,{"derivedFrom":[makeQuery(id+"F1.opExtrude","CAP_FACE",FACE,{"disambiguationData":[OSD([sQuery(id+"F0.wireOp",EDGE,"E0.1"),sQuery(id+"F0.wireOp",EDGE,"E0.3"),sQuery(id+"F0.wireOp",EDGE,"E0.4"),sQuery(id+"F0.wireOp",EDGE,"E0.5"),sQuery(id+"F0.wireOp",EDGE,"E1.0"),sQuery(id+"F0.wireOp",EDGE,"E1.1"),sQuery(id+"F0.wireOp",EDGE,"E1.2"),sQuery(id+"F0.wireOp",EDGE,"E1.3"),sQuery(id+"F0.wireOp",EDGE,"E1.5"),sQuery(id+"F0.wireOp",EDGE,"E2.0"),sQuery(id+"F0.wireOp",EDGE,"E2.1"),sQuery(id+"F0.wireOp",EDGE,"E2.2"),sQuery(id+"F0.wireOp",EDGE,"E2.4"),sQuery(id+"F0.wireOp",EDGE,"E2.5"),sQuery(id+"F0.wireOp",EDGE,"E3.filletArc"),sQuery(id+"F0.wireOp",EDGE,"E4.filletArc"),sQuery(id+"F0.wireOp",EDGE,"E5.filletArc"),sQuery(id+"F0.wireOp",EDGE,"E6.filletArc"),sQuery(id+"F0.wireOp",EDGE,"E7.filletArc"),sQuery(id+"F0.wireOp",EDGE,"E8.filletArc"),sQuery(id+"F0.wireOp",EDGE,"E9.filletArc"),sQuery(id+"F0.wireOp",EDGE,"E10.filletArc"),sQuery(id+"F0.wireOp",EDGE,"E11.filletArc"),sQuery(id+"F0.wireOp",EDGE,"E12.filletArc"),sQuery(id+"F0.wireOp",EDGE,"E13.filletArc"),sQuery(id+"F0.wireOp",EDGE,"E14.filletArc"),sQuery(id+"F0.wireOp",EDGE,"E15.filletArc"),sQuery(id+"F0.wireOp",EDGE,"E16.filletArc"),subQ17,subQ16,subQ15,subQ14,subQ13,subQ12,subQ11,subQ10,subQ9,subQ8,subQ7,subQ6,subQ5,subQ4,subQ3,subQ2,subQ1,subQ0])],"isStart":true}),makeQuery(id+"F2.opExtrude","CAP_FACE",FACE,{"disambiguationData":[OSD([subQ17])],"isStart":true}),makeQuery(id+"F2.opExtrude","CAP_FACE",FACE,{"disambiguationData":[OSD([subQ16])],"isStart":true}),makeQuery(id+"F2.opExtrude","CAP_FACE",FACE,{"disambiguationData":[OSD([subQ15])],"isStart":true}),makeQuery(id+"F2.opExtrude","CAP_FACE",FACE,{"disambiguationData":[OSD([subQ14])],"isStart":true}),makeQuery(id+"F2.opExtrude","CAP_FACE",FACE,{"disambiguationData":[OSD([subQ13])],"isStart":true}),makeQuery(id+"F2.opExtrude","CAP_FACE",FACE,{"disambiguationData":[OSD([subQ12])],"isStart":true}),makeQuery(id+"F2.opExtrude","CAP_FACE",FACE,{"disambiguationData":[OSD([subQ11])],"isStart":true}),makeQuery(id+"F2.opExtrude","CAP_FACE",FACE,{"disambiguationData":[OSD([subQ10])],"isStart":true}),makeQuery(id+"F2.opExtrude","CAP_FACE",FACE,{"disambiguationData":[OSD([subQ9])],"isStart":true}),makeQuery(id+"F2.opExtrude","CAP_FACE",FACE,{"disambiguationData":[OSD([subQ8])],"isStart":true}),makeQuery(id+"F2.opExtrude","CAP_FACE",FACE,{"disambiguationData":[OSD([subQ7])],"isStart":true}),makeQuery(id+"F2.opExtrude","CAP_FACE",FACE,{"disambiguationData":[OSD([subQ6])],"isStart":true}),makeQuery(id+"F2.opExtrude","CAP_FACE",FACE,{"disambiguationData":[OSD([subQ5])],"isStart":true}),makeQuery(id+"F2.opExtrude","CAP_FACE",FACE,{"disambiguationData":[OSD([subQ4])],"isStart":true}),makeQuery(id+"F2.opExtrude","CAP_FACE",FACE,{"disambiguationData":[OSD([subQ3])],"isStart":true}),makeQuery(id+"F2.opExtrude","CAP_FACE",FACE,{"disambiguationData":[OSD([subQ2])],"isStart":true}),makeQuery(id+"F2.opExtrude","CAP_FACE",FACE,{"disambiguationData":[OSD([subQ1])],"isStart":true}),makeQuery(id+"F2.opExtrude","CAP_FACE",FACE,{"disambiguationData":[OSD([subQ0])],"isStart":true})]});}
            extrude(context, id + "F8", {"entities" : qUnion([Q0]), "operationType" : NewBodyOperationType.ADD, "endBound" : BoundingType.UP_TO_SURFACE, "oppositeDirection" : true, "endBoundEntityFace" : qUnion([Q1]), "depth" : 25.4 * mm});
        }
        {
            var Q0;
            Q0=makeQuery(id+"F1.opExtrude","SWEPT_FACE",FACE,{"disambiguationData":[OSD([sQuery(id+"F0.wireOp",EDGE,"E1.0")])]});
            var Q1;
            Q1=makeQuery(id+"F1.opExtrude","SWEPT_FACE",FACE,{"disambiguationData":[OSD([sQuery(id+"F0.wireOp",EDGE,"E1.3")])]});
            cPlane(context, id + "F9", {"entities" : qUnion([Q0, Q1]), "cplaneType" : CPlaneType.MID_PLANE, "offset" : 25.4 * mm, "width" : 152.4 * mm, "height" : 152.4 * mm});
        }
        {
            var Q0;
            Q0=makeQuery(id+"F1.opExtrude","SWEPT_FACE",FACE,{"disambiguationData":[OSD([sQuery(id+"F0.wireOp",EDGE,"E1.1")])]});
            var Q1;
            Q1=makeQuery(id+"F1.opExtrude","SWEPT_FACE",FACE,{"disambiguationData":[OSD([sQuery(id+"F0.wireOp",EDGE,"E0.5")])]});
            cPlane(context, id + "F10", {"entities" : qUnion([Q0, Q1]), "cplaneType" : CPlaneType.MID_PLANE, "offset" : 25.4 * mm, "width" : 152.4 * mm, "height" : 152.4 * mm});
        }
        {
            var Q0;
            Q0=qCreatedBy(id+"F9.planeOp",FACE);
            var sketch = newSketch(context, id + "F11", { "sketchPlane" : qUnion([Q0])});
            skLineSegment(sketch, "E132", {"start": v(-217.77, 12.59) * mm, "end": v(-217.77, 74.92) * mm, "construction": true});
            skSolve(sketch);
        }
        {
            var Q0;
            {var subQ0=sQuery(id+"F7.wireOp",EDGE,"E130.right");var subQ1=sQuery(id+"F7.wireOp",EDGE,"E130.left");var subQ2=sQuery(id+"F7.wireOp",EDGE,"E130.top");var subQ3=sQuery(id+"F7.wireOp",EDGE,"E130.bottom");var subQ4=sQuery(id+"F0.wireOp",EDGE,"E25");var subQ5=sQuery(id+"F0.wireOp",EDGE,"E20");var subQ6=sQuery(id+"F0.wireOp",EDGE,"E21");var subQ7=sQuery(id+"F0.wireOp",EDGE,"E22");var subQ8=sQuery(id+"F0.wireOp",EDGE,"E23");var subQ9=sQuery(id+"F0.wireOp",EDGE,"E24");var subQ10=sQuery(id+"F0.wireOp",EDGE,"E37");var subQ11=sQuery(id+"F0.wireOp",EDGE,"E36");var subQ12=sQuery(id+"F0.wireOp",EDGE,"E35");var subQ13=sQuery(id+"F0.wireOp",EDGE,"E34");var subQ14=sQuery(id+"F0.wireOp",EDGE,"E33");var subQ15=sQuery(id+"F0.wireOp",EDGE,"E32");var subQ16=sQuery(id+"F0.wireOp",EDGE,"E31");var subQ17=sQuery(id+"F0.wireOp",EDGE,"E30");var subQ18=sQuery(id+"F0.wireOp",EDGE,"E29");var subQ19=sQuery(id+"F0.wireOp",EDGE,"E28");var subQ20=sQuery(id+"F0.wireOp",EDGE,"E27");var subQ21=sQuery(id+"F0.wireOp",EDGE,"E26");var subQ22=sQuery(id+"F0.wireOp",EDGE,"E16.filletArc");var subQ23=sQuery(id+"F0.wireOp",EDGE,"E15.filletArc");var subQ24=sQuery(id+"F0.wireOp",EDGE,"E14.filletArc");var subQ25=sQuery(id+"F0.wireOp",EDGE,"E13.filletArc");var subQ26=sQuery(id+"F0.wireOp",EDGE,"E12.filletArc");var subQ27=sQuery(id+"F0.wireOp",EDGE,"E11.filletArc");var subQ28=sQuery(id+"F0.wireOp",EDGE,"E10.filletArc");var subQ29=sQuery(id+"F0.wireOp",EDGE,"E9.filletArc");var subQ30=sQuery(id+"F0.wireOp",EDGE,"E8.filletArc");var subQ31=sQuery(id+"F0.wireOp",EDGE,"E7.filletArc");var subQ32=sQuery(id+"F0.wireOp",EDGE,"E6.filletArc");var subQ33=sQuery(id+"F0.wireOp",EDGE,"E5.filletArc");var subQ34=sQuery(id+"F0.wireOp",EDGE,"E4.filletArc");var subQ35=sQuery(id+"F0.wireOp",EDGE,"E3.filletArc");var subQ36=sQuery(id+"F0.wireOp",EDGE,"E2.5");var subQ37=sQuery(id+"F0.wireOp",EDGE,"E2.4");var subQ38=sQuery(id+"F0.wireOp",EDGE,"E2.2");var subQ39=sQuery(id+"F0.wireOp",EDGE,"E2.1");var subQ40=sQuery(id+"F0.wireOp",EDGE,"E2.0");var subQ41=sQuery(id+"F0.wireOp",EDGE,"E1.5");var subQ42=sQuery(id+"F0.wireOp",EDGE,"E1.3");var subQ43=sQuery(id+"F0.wireOp",EDGE,"E1.2");var subQ44=sQuery(id+"F0.wireOp",EDGE,"E1.1");var subQ45=sQuery(id+"F0.wireOp",EDGE,"E1.0");var subQ46=sQuery(id+"F0.wireOp",EDGE,"E0.5");var subQ47=sQuery(id+"F0.wireOp",EDGE,"E0.4");var subQ48=sQuery(id+"F0.wireOp",EDGE,"E0.3");var subQ49=sQuery(id+"F0.wireOp",EDGE,"E0.1");var subQ50=makeQuery(id+"F1.opExtrude","CAP_FACE",FACE,{"disambiguationData":[OSD([subQ49,subQ48,subQ47,subQ46,subQ45,subQ44,subQ43,subQ42,subQ41,subQ40,subQ39,subQ38,subQ37,subQ36,subQ35,subQ34,subQ33,subQ32,subQ31,subQ30,subQ29,subQ28,subQ27,subQ26,subQ25,subQ24,subQ23,subQ22,subQ5,subQ6,subQ7,subQ8,subQ9,subQ4,subQ21,subQ20,subQ19,subQ18,subQ17,subQ16,subQ15,subQ14,subQ13,subQ12,subQ11,subQ10])],"isStart":false});Q0=makeQuery(id+"FArHMtP67R58qOK_1.1.FbB5umPfR1j8SLP_1.5.F8.boolean.opBoolean","MERGE",FACE,{"derivedFrom":[makeQuery(id+"FArHMtP67R58qOK_1.1.FbB5umPfR1j8SLP_1.4.F8.boolean.opBoolean","MERGE",FACE,{"derivedFrom":[makeQuery(id+"FArHMtP67R58qOK_1.1.FbB5umPfR1j8SLP_1.3.F8.boolean.opBoolean","MERGE",FACE,{"derivedFrom":[makeQuery(id+"FArHMtP67R58qOK_1.1.FbB5umPfR1j8SLP_1.2.F8.boolean.opBoolean","MERGE",FACE,{"derivedFrom":[makeQuery(id+"FArHMtP67R58qOK_1.1.FbB5umPfR1j8SLP_1.1.F8.boolean.opBoolean","MERGE",FACE,{"derivedFrom":[makeQuery(id+"FArHMtP67R58qOK_1.1.F8.boolean.opBoolean","MERGE",FACE,{"derivedFrom":[makeQuery(id+"F0aKffUkCtTZm95_1.boolean.opBoolean","SPLIT",FACE,{"disambiguationData":[TD([makeQuery(id+"F1.opExtrude","SWEPT_FACE",FACE,{"disambiguationData":[OSD([subQ21])]})])],"derivedFrom":subQ50}),makeQuery(id+"FZtU8A5xYbT4ezZ_1.1.FbB5umPfR1j8SLP_1.5.F8.boolean.opBoolean","MERGE",FACE,{"derivedFrom":[makeQuery(id+"FZtU8A5xYbT4ezZ_1.1.FbB5umPfR1j8SLP_1.4.F8.boolean.opBoolean","MERGE",FACE,{"derivedFrom":[makeQuery(id+"FZtU8A5xYbT4ezZ_1.1.FbB5umPfR1j8SLP_1.3.F8.boolean.opBoolean","MERGE",FACE,{"derivedFrom":[makeQuery(id+"FZtU8A5xYbT4ezZ_1.1.FbB5umPfR1j8SLP_1.2.F8.boolean.opBoolean","MERGE",FACE,{"derivedFrom":[makeQuery(id+"FZtU8A5xYbT4ezZ_1.1.FbB5umPfR1j8SLP_1.1.F8.boolean.opBoolean","MERGE",FACE,{"derivedFrom":[makeQuery(id+"FZtU8A5xYbT4ezZ_1.1.F8.boolean.opBoolean","MERGE",FACE,{"derivedFrom":[makeQuery(id+"F0aKffUkCtTZm95_1.boolean.opBoolean","SPLIT",FACE,{"disambiguationData":[TD([makeQuery(id+"F1.opExtrude","SWEPT_FACE",FACE,{"disambiguationData":[OSD([subQ15])]})])],"derivedFrom":subQ50}),makeQuery(id+"FbB5umPfR1j8SLP_1.5.F8.boolean.opBoolean","MERGE",FACE,{"derivedFrom":[makeQuery(id+"FbB5umPfR1j8SLP_1.4.F8.boolean.opBoolean","MERGE",FACE,{"derivedFrom":[makeQuery(id+"FbB5umPfR1j8SLP_1.3.F8.boolean.opBoolean","MERGE",FACE,{"derivedFrom":[makeQuery(id+"FbB5umPfR1j8SLP_1.2.F8.boolean.opBoolean","MERGE",FACE,{"derivedFrom":[makeQuery(id+"FbB5umPfR1j8SLP_1.1.F8.boolean.opBoolean","MERGE",FACE,{"derivedFrom":[makeQuery(id+"F8.boolean.opBoolean","MERGE",FACE,{"derivedFrom":[makeQuery(id+"F0aKffUkCtTZm95_1.boolean.opBoolean","SPLIT",FACE,{"disambiguationData":[TD([makeQuery(id+"F1.opExtrude","SWEPT_FACE",FACE,{"disambiguationData":[OSD([subQ49])]})])],"derivedFrom":subQ50}),makeQuery(id+"F0aKffUkCtTZm95_1.boolean.opBoolean","SPLIT",FACE,{"disambiguationData":[TD([makeQuery(id+"F1.opExtrude","SWEPT_FACE",FACE,{"disambiguationData":[OSD([subQ5])]})])],"derivedFrom":subQ50}),makeQuery(id+"F8.opExtrude","CAP_FACE",FACE,{"disambiguationData":[OSD([subQ3,subQ2,subQ1,subQ0])],"isStart":true})]}),makeQuery(id+"FbB5umPfR1j8SLP_1.1.F8.opExtrude","CAP_FACE",FACE,{"disambiguationData":[OSD([subQ3,subQ2,subQ1,subQ0])],"isStart":true})]}),makeQuery(id+"FbB5umPfR1j8SLP_1.2.F8.opExtrude","CAP_FACE",FACE,{"disambiguationData":[OSD([subQ3,subQ2,subQ1,subQ0])],"isStart":true})]}),makeQuery(id+"FbB5umPfR1j8SLP_1.3.F8.opExtrude","CAP_FACE",FACE,{"disambiguationData":[OSD([subQ3,subQ2,subQ1,subQ0])],"isStart":true})]}),makeQuery(id+"FbB5umPfR1j8SLP_1.4.F8.opExtrude","CAP_FACE",FACE,{"disambiguationData":[OSD([subQ3,subQ2,subQ1,subQ0])],"isStart":true})]}),makeQuery(id+"FbB5umPfR1j8SLP_1.5.F8.opExtrude","CAP_FACE",FACE,{"disambiguationData":[OSD([subQ3,subQ2,subQ1,subQ0])],"isStart":true})]}),makeQuery(id+"FZtU8A5xYbT4ezZ_1.1.F8.opExtrude","CAP_FACE",FACE,{"disambiguationData":[OSD([subQ3,subQ2,subQ1,subQ0])],"isStart":true})]}),makeQuery(id+"FZtU8A5xYbT4ezZ_1.1.FbB5umPfR1j8SLP_1.1.F8.opExtrude","CAP_FACE",FACE,{"disambiguationData":[OSD([subQ3,subQ2,subQ1,subQ0])],"isStart":true})]}),makeQuery(id+"FZtU8A5xYbT4ezZ_1.1.FbB5umPfR1j8SLP_1.2.F8.opExtrude","CAP_FACE",FACE,{"disambiguationData":[OSD([subQ3,subQ2,subQ1,subQ0])],"isStart":true})]}),makeQuery(id+"FZtU8A5xYbT4ezZ_1.1.FbB5umPfR1j8SLP_1.3.F8.opExtrude","CAP_FACE",FACE,{"disambiguationData":[OSD([subQ3,subQ2,subQ1,subQ0])],"isStart":true})]}),makeQuery(id+"FZtU8A5xYbT4ezZ_1.1.FbB5umPfR1j8SLP_1.4.F8.opExtrude","CAP_FACE",FACE,{"disambiguationData":[OSD([subQ3,subQ2,subQ1,subQ0])],"isStart":true})]}),makeQuery(id+"FZtU8A5xYbT4ezZ_1.1.FbB5umPfR1j8SLP_1.5.F8.opExtrude","CAP_FACE",FACE,{"disambiguationData":[OSD([subQ3,subQ2,subQ1,subQ0])],"isStart":true})]}),makeQuery(id+"FArHMtP67R58qOK_1.1.F8.opExtrude","CAP_FACE",FACE,{"disambiguationData":[OSD([subQ3,subQ2,subQ1,subQ0])],"isStart":true})]}),makeQuery(id+"FArHMtP67R58qOK_1.1.FbB5umPfR1j8SLP_1.1.F8.opExtrude","CAP_FACE",FACE,{"disambiguationData":[OSD([subQ3,subQ2,subQ1,subQ0])],"isStart":true})]}),makeQuery(id+"FArHMtP67R58qOK_1.1.FbB5umPfR1j8SLP_1.2.F8.opExtrude","CAP_FACE",FACE,{"disambiguationData":[OSD([subQ3,subQ2,subQ1,subQ0])],"isStart":true})]}),makeQuery(id+"FArHMtP67R58qOK_1.1.FbB5umPfR1j8SLP_1.3.F8.opExtrude","CAP_FACE",FACE,{"disambiguationData":[OSD([subQ3,subQ2,subQ1,subQ0])],"isStart":true})]}),makeQuery(id+"FArHMtP67R58qOK_1.1.FbB5umPfR1j8SLP_1.4.F8.opExtrude","CAP_FACE",FACE,{"disambiguationData":[OSD([subQ3,subQ2,subQ1,subQ0])],"isStart":true})]}),makeQuery(id+"FArHMtP67R58qOK_1.1.FbB5umPfR1j8SLP_1.5.F8.opExtrude","CAP_FACE",FACE,{"disambiguationData":[OSD([subQ3,subQ2,subQ1,subQ0])],"isStart":true})]});}
            var sketch = newSketch(context, id + "F12", { "sketchPlane" : qUnion([Q0])});
            skLineSegment(sketch, "E133.bottom", {"start": v(-3.73, -87.63) * mm, "end": v(57.74, -87.63) * mm, "construction": true});
            skLineSegment(sketch, "E133.top", {"start": v(-3.73, -3.3) * mm, "end": v(57.74, -3.3) * mm, "construction": true});
            skLineSegment(sketch, "E133.left", {"start": v(-3.73, -87.63) * mm, "end": v(-3.73, -3.3) * mm, "construction": true});
            skLineSegment(sketch, "E133.right", {"start": v(57.74, -87.63) * mm, "end": v(57.74, -3.3) * mm, "construction": true});
            skLineSegment(sketch, "E134.bottom", {"start": v(-53, -3.3) * mm, "end": v(-16.43, -3.3) * mm, "construction": true});
            skLineSegment(sketch, "E134.top", {"start": v(-53, -41.4) * mm, "end": v(-16.43, -41.4) * mm, "construction": true});
            skLineSegment(sketch, "E134.left", {"start": v(-53, -3.3) * mm, "end": v(-53, -41.4) * mm, "construction": true});
            skLineSegment(sketch, "E134.right", {"start": v(-16.43, -3.3) * mm, "end": v(-16.43, -41.4) * mm, "construction": true});
            skCircle(sketch, "E135", {"center": v(-53, -3.3) * mm, "radius": 1.14 * mm});
            skCircle(sketch, "E136", {"center": v(-16.43, -3.3) * mm, "radius": 1.14 * mm});
            skCircle(sketch, "E137", {"center": v(-53, -41.4) * mm, "radius": 1.14 * mm});
            skCircle(sketch, "E138", {"center": v(-3.73, -87.63) * mm, "radius": 1.14 * mm});
            skCircle(sketch, "E139", {"center": v(57.74, -87.63) * mm, "radius": 1.14 * mm});
            skCircle(sketch, "E140", {"center": v(57.74, -3.3) * mm, "radius": 1.14 * mm});
            skCircle(sketch, "E141", {"center": v(-3.73, -3.3) * mm, "radius": 1.14 * mm});
            skCircle(sketch, "E142", {"center": v(-16.43, -41.4) * mm, "radius": 1.14 * mm});
            skSolve(sketch);
        }
        {
            var Q0;
            Q0 = qSketchRegion(id + "F12", true);
            var Q1;
            {var subQ0=sQuery(id+"F0.wireOp",EDGE,"E37");var subQ1=sQuery(id+"F0.wireOp",EDGE,"E36");var subQ2=sQuery(id+"F0.wireOp",EDGE,"E35");var subQ3=sQuery(id+"F0.wireOp",EDGE,"E34");var subQ4=sQuery(id+"F0.wireOp",EDGE,"E33");var subQ5=sQuery(id+"F0.wireOp",EDGE,"E32");var subQ6=sQuery(id+"F0.wireOp",EDGE,"E31");var subQ7=sQuery(id+"F0.wireOp",EDGE,"E30");var subQ8=sQuery(id+"F0.wireOp",EDGE,"E29");var subQ9=sQuery(id+"F0.wireOp",EDGE,"E28");var subQ10=sQuery(id+"F0.wireOp",EDGE,"E27");var subQ11=sQuery(id+"F0.wireOp",EDGE,"E26");var subQ12=sQuery(id+"F0.wireOp",EDGE,"E25");var subQ13=sQuery(id+"F0.wireOp",EDGE,"E24");var subQ14=sQuery(id+"F0.wireOp",EDGE,"E23");var subQ15=sQuery(id+"F0.wireOp",EDGE,"E22");var subQ16=sQuery(id+"F0.wireOp",EDGE,"E21");var subQ17=sQuery(id+"F0.wireOp",EDGE,"E20");var subQ18=sQuery(id+"F0.wireOp",EDGE,"E16.filletArc");var subQ19=sQuery(id+"F0.wireOp",EDGE,"E15.filletArc");var subQ20=sQuery(id+"F0.wireOp",EDGE,"E14.filletArc");var subQ21=sQuery(id+"F0.wireOp",EDGE,"E13.filletArc");var subQ22=sQuery(id+"F0.wireOp",EDGE,"E12.filletArc");var subQ23=sQuery(id+"F0.wireOp",EDGE,"E11.filletArc");var subQ24=sQuery(id+"F0.wireOp",EDGE,"E10.filletArc");var subQ25=sQuery(id+"F0.wireOp",EDGE,"E9.filletArc");var subQ26=sQuery(id+"F0.wireOp",EDGE,"E8.filletArc");var subQ27=sQuery(id+"F0.wireOp",EDGE,"E7.filletArc");var subQ28=sQuery(id+"F0.wireOp",EDGE,"E6.filletArc");var subQ29=sQuery(id+"F0.wireOp",EDGE,"E5.filletArc");var subQ30=sQuery(id+"F0.wireOp",EDGE,"E4.filletArc");var subQ31=sQuery(id+"F0.wireOp",EDGE,"E3.filletArc");var subQ32=sQuery(id+"F0.wireOp",EDGE,"E2.5");var subQ33=sQuery(id+"F0.wireOp",EDGE,"E2.4");var subQ34=sQuery(id+"F0.wireOp",EDGE,"E2.2");var subQ35=sQuery(id+"F0.wireOp",EDGE,"E2.1");var subQ36=sQuery(id+"F0.wireOp",EDGE,"E2.0");var subQ37=sQuery(id+"F0.wireOp",EDGE,"E1.5");var subQ38=sQuery(id+"F0.wireOp",EDGE,"E1.3");var subQ39=sQuery(id+"F0.wireOp",EDGE,"E1.2");var subQ40=sQuery(id+"F0.wireOp",EDGE,"E1.1");var subQ41=sQuery(id+"F0.wireOp",EDGE,"E1.0");var subQ42=sQuery(id+"F0.wireOp",EDGE,"E0.5");var subQ43=sQuery(id+"F0.wireOp",EDGE,"E0.4");var subQ44=sQuery(id+"F0.wireOp",EDGE,"E0.3");var subQ45=sQuery(id+"F0.wireOp",EDGE,"E0.1");Q1=makeQuery(id+"FArHMtP67R58qOK_1.1.FbB5umPfR1j8SLP_1.5.F8.boolean.opBoolean","MERGE",FACE,{"derivedFrom":[makeQuery(id+"FArHMtP67R58qOK_1.1.FbB5umPfR1j8SLP_1.4.F8.boolean.opBoolean","MERGE",FACE,{"derivedFrom":[makeQuery(id+"FArHMtP67R58qOK_1.1.FbB5umPfR1j8SLP_1.3.F8.boolean.opBoolean","MERGE",FACE,{"derivedFrom":[makeQuery(id+"FArHMtP67R58qOK_1.1.FbB5umPfR1j8SLP_1.2.F8.boolean.opBoolean","MERGE",FACE,{"derivedFrom":[makeQuery(id+"FArHMtP67R58qOK_1.1.FbB5umPfR1j8SLP_1.1.F8.boolean.opBoolean","MERGE",FACE,{"derivedFrom":[makeQuery(id+"FArHMtP67R58qOK_1.1.F8.boolean.opBoolean","MERGE",FACE,{"derivedFrom":[makeQuery(id+"FZtU8A5xYbT4ezZ_1.1.FbB5umPfR1j8SLP_1.5.F8.boolean.opBoolean","MERGE",FACE,{"derivedFrom":[makeQuery(id+"FZtU8A5xYbT4ezZ_1.1.FbB5umPfR1j8SLP_1.4.F8.boolean.opBoolean","MERGE",FACE,{"derivedFrom":[makeQuery(id+"FZtU8A5xYbT4ezZ_1.1.FbB5umPfR1j8SLP_1.3.F8.boolean.opBoolean","MERGE",FACE,{"derivedFrom":[makeQuery(id+"FZtU8A5xYbT4ezZ_1.1.FbB5umPfR1j8SLP_1.2.F8.boolean.opBoolean","MERGE",FACE,{"derivedFrom":[makeQuery(id+"FZtU8A5xYbT4ezZ_1.1.FbB5umPfR1j8SLP_1.1.F8.boolean.opBoolean","MERGE",FACE,{"derivedFrom":[makeQuery(id+"FZtU8A5xYbT4ezZ_1.1.F8.boolean.opBoolean","MERGE",FACE,{"derivedFrom":[makeQuery(id+"FbB5umPfR1j8SLP_1.5.F8.boolean.opBoolean","MERGE",FACE,{"derivedFrom":[makeQuery(id+"FbB5umPfR1j8SLP_1.4.F8.boolean.opBoolean","MERGE",FACE,{"derivedFrom":[makeQuery(id+"FbB5umPfR1j8SLP_1.3.F8.boolean.opBoolean","MERGE",FACE,{"derivedFrom":[makeQuery(id+"FbB5umPfR1j8SLP_1.2.F8.boolean.opBoolean","MERGE",FACE,{"derivedFrom":[makeQuery(id+"FbB5umPfR1j8SLP_1.1.F8.boolean.opBoolean","MERGE",FACE,{"derivedFrom":[makeQuery(id+"F8.boolean.opBoolean","MERGE",FACE,{"derivedFrom":[makeQuery(id+"F2.boolean.opBoolean","MERGE",FACE,{"derivedFrom":[makeQuery(id+"F1.opExtrude","CAP_FACE",FACE,{"disambiguationData":[OSD([subQ45,subQ44,subQ43,subQ42,subQ41,subQ40,subQ39,subQ38,subQ37,subQ36,subQ35,subQ34,subQ33,subQ32,subQ31,subQ30,subQ29,subQ28,subQ27,subQ26,subQ25,subQ24,subQ23,subQ22,subQ21,subQ20,subQ19,subQ18,subQ17,subQ16,subQ15,subQ14,subQ13,subQ12,subQ11,subQ10,subQ9,subQ8,subQ7,subQ6,subQ5,subQ4,subQ3,subQ2,subQ1,subQ0])],"isStart":true}),makeQuery(id+"F2.opExtrude","CAP_FACE",FACE,{"disambiguationData":[OSD([subQ17])],"isStart":true}),makeQuery(id+"F2.opExtrude","CAP_FACE",FACE,{"disambiguationData":[OSD([subQ16])],"isStart":true}),makeQuery(id+"F2.opExtrude","CAP_FACE",FACE,{"disambiguationData":[OSD([subQ15])],"isStart":true}),makeQuery(id+"F2.opExtrude","CAP_FACE",FACE,{"disambiguationData":[OSD([subQ14])],"isStart":true}),makeQuery(id+"F2.opExtrude","CAP_FACE",FACE,{"disambiguationData":[OSD([subQ13])],"isStart":true}),makeQuery(id+"F2.opExtrude","CAP_FACE",FACE,{"disambiguationData":[OSD([subQ12])],"isStart":true}),makeQuery(id+"F2.opExtrude","CAP_FACE",FACE,{"disambiguationData":[OSD([subQ11])],"isStart":true}),makeQuery(id+"F2.opExtrude","CAP_FACE",FACE,{"disambiguationData":[OSD([subQ10])],"isStart":true}),makeQuery(id+"F2.opExtrude","CAP_FACE",FACE,{"disambiguationData":[OSD([subQ9])],"isStart":true}),makeQuery(id+"F2.opExtrude","CAP_FACE",FACE,{"disambiguationData":[OSD([subQ8])],"isStart":true}),makeQuery(id+"F2.opExtrude","CAP_FACE",FACE,{"disambiguationData":[OSD([subQ7])],"isStart":true}),makeQuery(id+"F2.opExtrude","CAP_FACE",FACE,{"disambiguationData":[OSD([subQ6])],"isStart":true}),makeQuery(id+"F2.opExtrude","CAP_FACE",FACE,{"disambiguationData":[OSD([subQ5])],"isStart":true}),makeQuery(id+"F2.opExtrude","CAP_FACE",FACE,{"disambiguationData":[OSD([subQ4])],"isStart":true}),makeQuery(id+"F2.opExtrude","CAP_FACE",FACE,{"disambiguationData":[OSD([subQ3])],"isStart":true}),makeQuery(id+"F2.opExtrude","CAP_FACE",FACE,{"disambiguationData":[OSD([subQ2])],"isStart":true}),makeQuery(id+"F2.opExtrude","CAP_FACE",FACE,{"disambiguationData":[OSD([subQ1])],"isStart":true}),makeQuery(id+"F2.opExtrude","CAP_FACE",FACE,{"disambiguationData":[OSD([subQ0])],"isStart":true})]}),makeQuery(id+"F8.opExtrude","CAP_FACE",FACE,{"disambiguationData":[OSD([subQ45,subQ44,subQ43,subQ42,subQ41,subQ40,subQ39,subQ38,subQ37,subQ36,subQ35,subQ34,subQ33,subQ32,subQ31,subQ30,subQ29,subQ28,subQ27,subQ26,subQ25,subQ24,subQ23,subQ22,subQ21,subQ20,subQ19,subQ18,subQ17,subQ16,subQ15,subQ14,subQ13,subQ12,subQ11,subQ10,subQ9,subQ8,subQ7,subQ6,subQ5,subQ4,subQ3,subQ2,subQ1,subQ0])],"isStart":false})]}),makeQuery(id+"FbB5umPfR1j8SLP_1.1.F8.opExtrude","CAP_FACE",FACE,{"disambiguationData":[OSD([subQ45,subQ44,subQ43,subQ42,subQ41,subQ40,subQ39,subQ38,subQ37,subQ36,subQ35,subQ34,subQ33,subQ32,subQ31,subQ30,subQ29,subQ28,subQ27,subQ26,subQ25,subQ24,subQ23,subQ22,subQ21,subQ20,subQ19,subQ18,subQ17,subQ16,subQ15,subQ14,subQ13,subQ12,subQ11,subQ10,subQ9,subQ8,subQ7,subQ6,subQ5,subQ4,subQ3,subQ2,subQ1,subQ0])],"isStart":false})]}),makeQuery(id+"FbB5umPfR1j8SLP_1.2.F8.opExtrude","CAP_FACE",FACE,{"disambiguationData":[OSD([subQ45,subQ44,subQ43,subQ42,subQ41,subQ40,subQ39,subQ38,subQ37,subQ36,subQ35,subQ34,subQ33,subQ32,subQ31,subQ30,subQ29,subQ28,subQ27,subQ26,subQ25,subQ24,subQ23,subQ22,subQ21,subQ20,subQ19,subQ18,subQ17,subQ16,subQ15,subQ14,subQ13,subQ12,subQ11,subQ10,subQ9,subQ8,subQ7,subQ6,subQ5,subQ4,subQ3,subQ2,subQ1,subQ0])],"isStart":false})]}),makeQuery(id+"FbB5umPfR1j8SLP_1.3.F8.opExtrude","CAP_FACE",FACE,{"disambiguationData":[OSD([subQ45,subQ44,subQ43,subQ42,subQ41,subQ40,subQ39,subQ38,subQ37,subQ36,subQ35,subQ34,subQ33,subQ32,subQ31,subQ30,subQ29,subQ28,subQ27,subQ26,subQ25,subQ24,subQ23,subQ22,subQ21,subQ20,subQ19,subQ18,subQ17,subQ16,subQ15,subQ14,subQ13,subQ12,subQ11,subQ10,subQ9,subQ8,subQ7,subQ6,subQ5,subQ4,subQ3,subQ2,subQ1,subQ0])],"isStart":false})]}),makeQuery(id+"FbB5umPfR1j8SLP_1.4.F8.opExtrude","CAP_FACE",FACE,{"disambiguationData":[OSD([subQ45,subQ44,subQ43,subQ42,subQ41,subQ40,subQ39,subQ38,subQ37,subQ36,subQ35,subQ34,subQ33,subQ32,subQ31,subQ30,subQ29,subQ28,subQ27,subQ26,subQ25,subQ24,subQ23,subQ22,subQ21,subQ20,subQ19,subQ18,subQ17,subQ16,subQ15,subQ14,subQ13,subQ12,subQ11,subQ10,subQ9,subQ8,subQ7,subQ6,subQ5,subQ4,subQ3,subQ2,subQ1,subQ0])],"isStart":false})]}),makeQuery(id+"FbB5umPfR1j8SLP_1.5.F8.opExtrude","CAP_FACE",FACE,{"disambiguationData":[OSD([subQ45,subQ44,subQ43,subQ42,subQ41,subQ40,subQ39,subQ38,subQ37,subQ36,subQ35,subQ34,subQ33,subQ32,subQ31,subQ30,subQ29,subQ28,subQ27,subQ26,subQ25,subQ24,subQ23,subQ22,subQ21,subQ20,subQ19,subQ18,subQ17,subQ16,subQ15,subQ14,subQ13,subQ12,subQ11,subQ10,subQ9,subQ8,subQ7,subQ6,subQ5,subQ4,subQ3,subQ2,subQ1,subQ0])],"isStart":false})]}),makeQuery(id+"FZtU8A5xYbT4ezZ_1.1.F8.opExtrude","CAP_FACE",FACE,{"disambiguationData":[OSD([subQ45,subQ44,subQ43,subQ42,subQ41,subQ40,subQ39,subQ38,subQ37,subQ36,subQ35,subQ34,subQ33,subQ32,subQ31,subQ30,subQ29,subQ28,subQ27,subQ26,subQ25,subQ24,subQ23,subQ22,subQ21,subQ20,subQ19,subQ18,subQ17,subQ16,subQ15,subQ14,subQ13,subQ12,subQ11,subQ10,subQ9,subQ8,subQ7,subQ6,subQ5,subQ4,subQ3,subQ2,subQ1,subQ0])],"isStart":false})]}),makeQuery(id+"FZtU8A5xYbT4ezZ_1.1.FbB5umPfR1j8SLP_1.1.F8.opExtrude","CAP_FACE",FACE,{"disambiguationData":[OSD([subQ45,subQ44,subQ43,subQ42,subQ41,subQ40,subQ39,subQ38,subQ37,subQ36,subQ35,subQ34,subQ33,subQ32,subQ31,subQ30,subQ29,subQ28,subQ27,subQ26,subQ25,subQ24,subQ23,subQ22,subQ21,subQ20,subQ19,subQ18,subQ17,subQ16,subQ15,subQ14,subQ13,subQ12,subQ11,subQ10,subQ9,subQ8,subQ7,subQ6,subQ5,subQ4,subQ3,subQ2,subQ1,subQ0])],"isStart":false})]}),makeQuery(id+"FZtU8A5xYbT4ezZ_1.1.FbB5umPfR1j8SLP_1.2.F8.opExtrude","CAP_FACE",FACE,{"disambiguationData":[OSD([subQ45,subQ44,subQ43,subQ42,subQ41,subQ40,subQ39,subQ38,subQ37,subQ36,subQ35,subQ34,subQ33,subQ32,subQ31,subQ30,subQ29,subQ28,subQ27,subQ26,subQ25,subQ24,subQ23,subQ22,subQ21,subQ20,subQ19,subQ18,subQ17,subQ16,subQ15,subQ14,subQ13,subQ12,subQ11,subQ10,subQ9,subQ8,subQ7,subQ6,subQ5,subQ4,subQ3,subQ2,subQ1,subQ0])],"isStart":false})]}),makeQuery(id+"FZtU8A5xYbT4ezZ_1.1.FbB5umPfR1j8SLP_1.3.F8.opExtrude","CAP_FACE",FACE,{"disambiguationData":[OSD([subQ45,subQ44,subQ43,subQ42,subQ41,subQ40,subQ39,subQ38,subQ37,subQ36,subQ35,subQ34,subQ33,subQ32,subQ31,subQ30,subQ29,subQ28,subQ27,subQ26,subQ25,subQ24,subQ23,subQ22,subQ21,subQ20,subQ19,subQ18,subQ17,subQ16,subQ15,subQ14,subQ13,subQ12,subQ11,subQ10,subQ9,subQ8,subQ7,subQ6,subQ5,subQ4,subQ3,subQ2,subQ1,subQ0])],"isStart":false})]}),makeQuery(id+"FZtU8A5xYbT4ezZ_1.1.FbB5umPfR1j8SLP_1.4.F8.opExtrude","CAP_FACE",FACE,{"disambiguationData":[OSD([subQ45,subQ44,subQ43,subQ42,subQ41,subQ40,subQ39,subQ38,subQ37,subQ36,subQ35,subQ34,subQ33,subQ32,subQ31,subQ30,subQ29,subQ28,subQ27,subQ26,subQ25,subQ24,subQ23,subQ22,subQ21,subQ20,subQ19,subQ18,subQ17,subQ16,subQ15,subQ14,subQ13,subQ12,subQ11,subQ10,subQ9,subQ8,subQ7,subQ6,subQ5,subQ4,subQ3,subQ2,subQ1,subQ0])],"isStart":false})]}),makeQuery(id+"FZtU8A5xYbT4ezZ_1.1.FbB5umPfR1j8SLP_1.5.F8.opExtrude","CAP_FACE",FACE,{"disambiguationData":[OSD([subQ45,subQ44,subQ43,subQ42,subQ41,subQ40,subQ39,subQ38,subQ37,subQ36,subQ35,subQ34,subQ33,subQ32,subQ31,subQ30,subQ29,subQ28,subQ27,subQ26,subQ25,subQ24,subQ23,subQ22,subQ21,subQ20,subQ19,subQ18,subQ17,subQ16,subQ15,subQ14,subQ13,subQ12,subQ11,subQ10,subQ9,subQ8,subQ7,subQ6,subQ5,subQ4,subQ3,subQ2,subQ1,subQ0])],"isStart":false})]}),makeQuery(id+"FArHMtP67R58qOK_1.1.F8.opExtrude","CAP_FACE",FACE,{"disambiguationData":[OSD([subQ45,subQ44,subQ43,subQ42,subQ41,subQ40,subQ39,subQ38,subQ37,subQ36,subQ35,subQ34,subQ33,subQ32,subQ31,subQ30,subQ29,subQ28,subQ27,subQ26,subQ25,subQ24,subQ23,subQ22,subQ21,subQ20,subQ19,subQ18,subQ17,subQ16,subQ15,subQ14,subQ13,subQ12,subQ11,subQ10,subQ9,subQ8,subQ7,subQ6,subQ5,subQ4,subQ3,subQ2,subQ1,subQ0])],"isStart":false})]}),makeQuery(id+"FArHMtP67R58qOK_1.1.FbB5umPfR1j8SLP_1.1.F8.opExtrude","CAP_FACE",FACE,{"disambiguationData":[OSD([subQ45,subQ44,subQ43,subQ42,subQ41,subQ40,subQ39,subQ38,subQ37,subQ36,subQ35,subQ34,subQ33,subQ32,subQ31,subQ30,subQ29,subQ28,subQ27,subQ26,subQ25,subQ24,subQ23,subQ22,subQ21,subQ20,subQ19,subQ18,subQ17,subQ16,subQ15,subQ14,subQ13,subQ12,subQ11,subQ10,subQ9,subQ8,subQ7,subQ6,subQ5,subQ4,subQ3,subQ2,subQ1,subQ0])],"isStart":false})]}),makeQuery(id+"FArHMtP67R58qOK_1.1.FbB5umPfR1j8SLP_1.2.F8.opExtrude","CAP_FACE",FACE,{"disambiguationData":[OSD([subQ45,subQ44,subQ43,subQ42,subQ41,subQ40,subQ39,subQ38,subQ37,subQ36,subQ35,subQ34,subQ33,subQ32,subQ31,subQ30,subQ29,subQ28,subQ27,subQ26,subQ25,subQ24,subQ23,subQ22,subQ21,subQ20,subQ19,subQ18,subQ17,subQ16,subQ15,subQ14,subQ13,subQ12,subQ11,subQ10,subQ9,subQ8,subQ7,subQ6,subQ5,subQ4,subQ3,subQ2,subQ1,subQ0])],"isStart":false})]}),makeQuery(id+"FArHMtP67R58qOK_1.1.FbB5umPfR1j8SLP_1.3.F8.opExtrude","CAP_FACE",FACE,{"disambiguationData":[OSD([subQ45,subQ44,subQ43,subQ42,subQ41,subQ40,subQ39,subQ38,subQ37,subQ36,subQ35,subQ34,subQ33,subQ32,subQ31,subQ30,subQ29,subQ28,subQ27,subQ26,subQ25,subQ24,subQ23,subQ22,subQ21,subQ20,subQ19,subQ18,subQ17,subQ16,subQ15,subQ14,subQ13,subQ12,subQ11,subQ10,subQ9,subQ8,subQ7,subQ6,subQ5,subQ4,subQ3,subQ2,subQ1,subQ0])],"isStart":false})]}),makeQuery(id+"FArHMtP67R58qOK_1.1.FbB5umPfR1j8SLP_1.4.F8.opExtrude","CAP_FACE",FACE,{"disambiguationData":[OSD([subQ45,subQ44,subQ43,subQ42,subQ41,subQ40,subQ39,subQ38,subQ37,subQ36,subQ35,subQ34,subQ33,subQ32,subQ31,subQ30,subQ29,subQ28,subQ27,subQ26,subQ25,subQ24,subQ23,subQ22,subQ21,subQ20,subQ19,subQ18,subQ17,subQ16,subQ15,subQ14,subQ13,subQ12,subQ11,subQ10,subQ9,subQ8,subQ7,subQ6,subQ5,subQ4,subQ3,subQ2,subQ1,subQ0])],"isStart":false})]}),makeQuery(id+"FArHMtP67R58qOK_1.1.FbB5umPfR1j8SLP_1.5.F8.opExtrude","CAP_FACE",FACE,{"disambiguationData":[OSD([subQ45,subQ44,subQ43,subQ42,subQ41,subQ40,subQ39,subQ38,subQ37,subQ36,subQ35,subQ34,subQ33,subQ32,subQ31,subQ30,subQ29,subQ28,subQ27,subQ26,subQ25,subQ24,subQ23,subQ22,subQ21,subQ20,subQ19,subQ18,subQ17,subQ16,subQ15,subQ14,subQ13,subQ12,subQ11,subQ10,subQ9,subQ8,subQ7,subQ6,subQ5,subQ4,subQ3,subQ2,subQ1,subQ0])],"isStart":false})]});}
            extrude(context, id + "F13", {"entities" : qUnion([Q0]), "operationType" : NewBodyOperationType.REMOVE, "endBound" : BoundingType.UP_TO_SURFACE, "oppositeDirection" : true, "endBoundEntityFace" : qUnion([Q1]), "depth" : 25.4 * mm});
        }
    });
